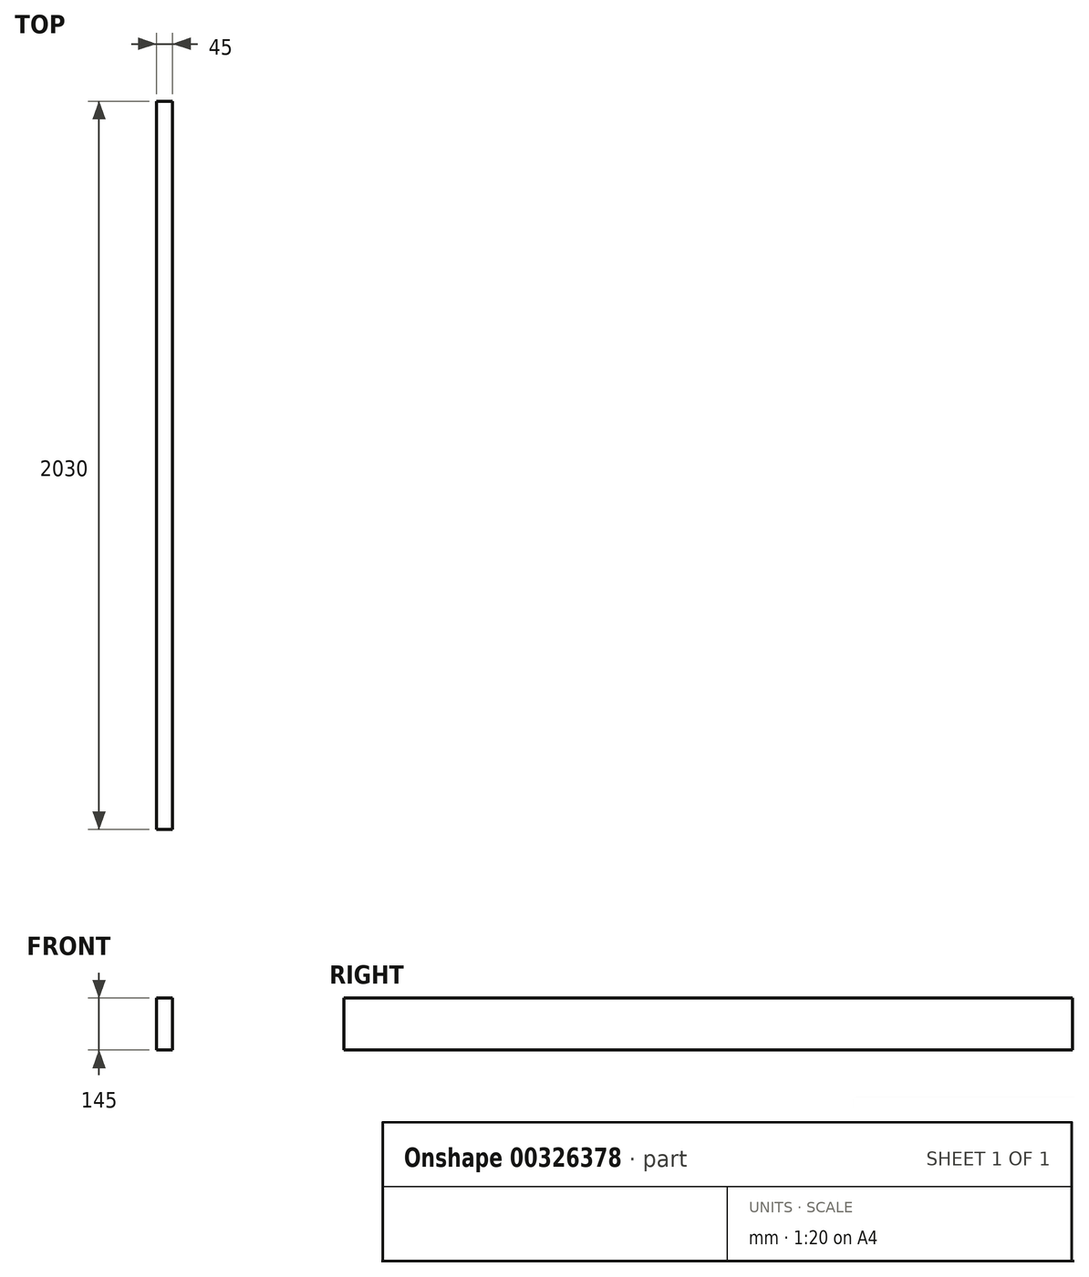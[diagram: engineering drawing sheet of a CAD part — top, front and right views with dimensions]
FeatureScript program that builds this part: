
annotation { "Feature Type Name" : "Feature", "Feature Type Description" : "" }
export const myFeature = defineFeature(function(context is Context, id is Id, definition is map)
    precondition{}
    {
        {
            var Q0;
            Q0=qCreatedBy(makeId("Front.planeOp"),FACE);
            var sketch = newSketch(context, id + "F0", { "sketchPlane" : qUnion([Q0])});
            skLineSegment(sketch, "E0.bottom", {"start": v(0, 0) * mm, "end": v(45, 0) * mm});
            skLineSegment(sketch, "E0.top", {"start": v(0, 145) * mm, "end": v(45, 145) * mm});
            skLineSegment(sketch, "E0.left", {"start": v(0, 0) * mm, "end": v(0, 145) * mm});
            skLineSegment(sketch, "E0.right", {"start": v(45, 0) * mm, "end": v(45, 145) * mm});
            skSolve(sketch);
        }
        {
            var Q0;
            Q0=makeQuery(id+"F0.imprint","IMPRINT",FACE,{"disambiguationData":[TD([[makeQuery(id+"F0.imprint","IMPRINT",EDGE,{"derivedFrom":sQuery(id+"F0.wireOp",EDGE,"E0.bottom")}),1.0]])]});
            extrude(context, id + "F1", {"entities" : qUnion([Q0]), "depth" : 2030 * mm});
        }
    });
